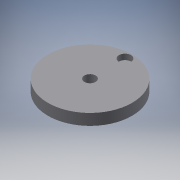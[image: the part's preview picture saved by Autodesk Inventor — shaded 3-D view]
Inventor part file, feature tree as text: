
AUTODESK INVENTOR PART (.ipt)
format: ipt  version: 2016 (Build 200138000, 138)  size: 130,048 bytes
history: native  units: mm
features: extrude x4, sketch x4, projected_geometry x1
ambient origin geometry x8: Origin, YZ Plane, XZ Plane, XY Plane, X Axis, Y Axis, Z Axis, Center Point
bodies: Solid1 (feature_tree)
feature tree (9):
  extrude  "Extrusion1"  Depth=8.0mm
  extrude  "Extrusion2"  Depth=8.0mm
  extrude  "Extrusion3"  Depth=4.0mm TaperAngle=0.0deg
  extrude  "Extrusion4"  Depth=25.0mm
  sketch  "Sketch1"  dims[d0=60.0mm d1=8.0mm]
  sketch  "Sketch2"  dims[d2=8.0mm d3=0.0mm d4=8.5mm]
  sketch  "Sketch3"  dims[d5=25.0mm d6=4.0mm d7=0.0mm]
  sketch  "Sketch4"  dims[d8=10.0mm d9=25.0mm d10=6.0mm d11=0.0mm d12=2.8mm d13=6.0mm d14=0.0mm]
  projected_geometry  "Projected Loop1"
